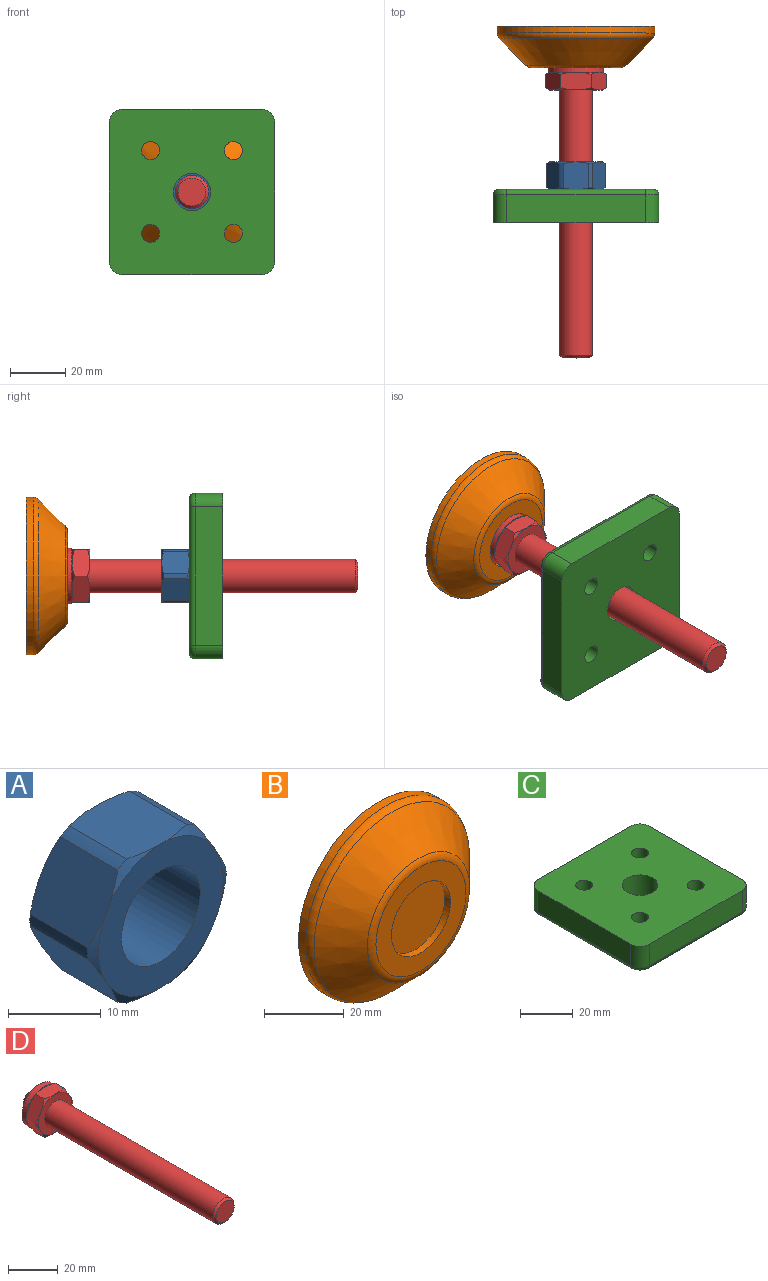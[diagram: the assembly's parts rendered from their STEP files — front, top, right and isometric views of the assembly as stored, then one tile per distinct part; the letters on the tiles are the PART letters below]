
ASSEMBLY  parts=4 mates=3
PART A: 27 faces, bbox 21.1x10x21.1 mm
  f0: cylinder r=6mm len=12mm, axis (0,-1,0), area 377mm2, adj f23,f24
  f1: plane 10x7.95mm, normal (0.87,0,0.5), area 88mm2, adj f2,f3,f4,f5,f19,f21
  f2: cone r=5.28mm half-angle=60deg, axis (0,-1,0), area 5.2mm2, adj f1,f4,f6,f24
  f3: cone r=5.28mm half-angle=60deg, axis (0,-1,0), area 5.2mm2, adj f1,f21,f22,f24
  f4: cylinder r=10.55mm len=8.79mm, axis (0,-1,0), area 13.7mm2, adj f1,f2,f5,f6
  f5: cone r=5.28mm half-angle=60deg, axis (0,1,0), area 5.2mm2, adj f1,f4,f6,f23
  f6: plane 10x7.95mm, normal (0.87,0,-0.5), area 88mm2, adj f2,f4,f5,f7,f8,f9
  f7: cone r=5.28mm half-angle=60deg, axis (0,-1,0), area 5.2mm2, adj f6,f8,f10,f24
  f8: cylinder r=10.55mm len=8.79mm, axis (0,-1,0), area 13.7mm2, adj f6,f7,f9,f10
  f9: cone r=5.28mm half-angle=60deg, axis (0,1,0), area 5.2mm2, adj f6,f8,f10,f23
  f10: plane 10x9.18mm, normal (0,0,-1), area 88mm2, adj f7,f8,f9,f11,f12,f13
  f11: cone r=5.28mm half-angle=60deg, axis (0,-1,0), area 5.2mm2, adj f10,f12,f14,f24
  f12: cylinder r=10.55mm len=8.79mm, axis (0,-1,0), area 13.7mm2, adj f10,f11,f13,f14
  f13: cone r=5.28mm half-angle=60deg, axis (0,1,0), area 5.2mm2, adj f10,f12,f14,f23
  f14: plane 10x7.95mm, normal (-0.87,0,-0.5), area 88mm2, adj f11,f12,f13,f15,f16,f17
  f15: cone r=5.28mm half-angle=60deg, axis (0,-1,0), area 5.2mm2, adj f14,f16,f18,f24
  f16: cylinder r=10.55mm len=8.79mm, axis (0,-1,0), area 13.7mm2, adj f14,f15,f17,f18
  f17: cone r=5.28mm half-angle=60deg, axis (0,1,0), area 5.2mm2, adj f14,f16,f18,f23
  f18: plane 10x7.95mm, normal (-0.87,0,0.5), area 88mm2, adj f15,f16,f17,f20,f25,f26
  f19: cone r=5.28mm half-angle=60deg, axis (0,1,0), area 5.2mm2, adj f1,f21,f22,f23
  f20: cone r=5.28mm half-angle=60deg, axis (0,1,0), area 5.2mm2, adj f18,f22,f23,f26
  f21: cylinder r=10.55mm len=8.79mm, axis (0,-1,0), area 13.7mm2, adj f1,f3,f19,f22
  f22: plane 10x9.18mm, normal (0,0,1), area 88mm2, adj f3,f19,f20,f21,f25,f26
  f23: plane 19x19mm, normal (0,-1,0), area 170.4mm2, adj f0,f5,f9,f13,f17,f19,f20
  f24: plane 19x19mm, normal (0,1,0), area 170.4mm2, adj f0,f2,f3,f7,f11,f15,f25
  f25: cone r=5.28mm half-angle=60deg, axis (0,-1,0), area 5.2mm2, adj f18,f22,f24,f26
  f26: cylinder r=10.55mm len=8.79mm, axis (0,-1,0), area 13.7mm2, adj f18,f20,f22,f25
PART B: 8 faces, bbox 61.7x15x61.7 mm
  f0: cylinder r=28.5mm len=57mm, axis (0,1,0), area 449mm2, adj f1,f7
  f1: torus R=25.5mm, axis (0,1,0), area 417.5mm2, adj f0,f2
  f2: cone r=22.88mm half-angle=45deg, axis (0,1,0), area 1929.5mm2, adj f1,f3
  f3: torus R=16.01mm, axis (0,1,0), area 253.5mm2, adj f2,f6
  f4: cylinder r=10.5mm len=21mm, axis (0,1,0), area 131.9mm2, adj f5,f6
  f5: plane 21x21mm, normal (0,-1,0), area 346.4mm2, adj f4
  f6: plane 32.01x32.01mm, normal (0,-1,0), area 458.6mm2, adj f3,f4
  f7: plane 57x57mm, normal (0,1,0), area 2551.8mm2, adj f0
PART C: 31 faces, bbox 60.8x60.8x12 mm
  f0: cylinder r=3.25mm len=6.5mm, axis (0,0,-1), area 122.5mm2, adj f3,f7
  f1: plane 50x10mm, normal (0,-1,0), area 500mm2, adj f3,f5,f8,f20
  f2: plane 50x10mm, normal (1,0,0), area 500mm2, adj f3,f5,f10,f13
  f3: plane 60x60mm, normal (0,0,1), area 3302.7mm2, adj f0,f1,f2,f5,f11,f12,f13,f18
  f4: plane 56x56mm, normal (0,0,-1), area 2605mm2, adj f6,f8,f9,f10,f14,f16,f17,f21
  f5: cylinder r=5mm len=10mm, axis (0,0,1), area 78.5mm2, adj f1,f2,f3,f9
  f6: cylinder r=5.5mm len=11mm, axis (0,0,-1), area 207.3mm2, adj f4,f7
  f7: plane 11x11mm, normal (0,0,-1), area 61.9mm2, adj f0,f6
  f8: cylinder r=2mm len=50mm, axis (1,0,0), area 157.1mm2, adj f1,f4,f9,f24
  f9: torus R=3mm, axis (0,0,1), area 21.1mm2, adj f4,f5,f8,f10
  f10: cylinder r=2mm len=50mm, axis (0,1,0), area 157.1mm2, adj f2,f4,f9,f16
  f11: cylinder r=3.25mm len=6.5mm, axis (0,0,-1), area 122.5mm2, adj f3,f15
  f12: plane 50x10mm, normal (0,1,0), area 500mm2, adj f3,f13,f17,f26
  f13: cylinder r=5mm len=10mm, axis (0,0,1), area 78.5mm2, adj f2,f3,f12,f16
  f14: cylinder r=5.5mm len=11mm, axis (0,0,-1), area 207.3mm2, adj f4,f15
  f15: plane 11x11mm, normal (0,0,-1), area 61.9mm2, adj f11,f14
  f16: torus R=3mm, axis (0,0,1), area 21.1mm2, adj f4,f10,f13,f17
  f17: cylinder r=2mm len=50mm, axis (-1,0,0), area 157.1mm2, adj f4,f12,f16,f29
  f18: cylinder r=3.25mm len=6.5mm, axis (0,0,-1), area 122.5mm2, adj f3,f22
  f19: plane 50x10mm, normal (-1,0,0), area 500mm2, adj f3,f20,f23,f26
  f20: cylinder r=5mm len=10mm, axis (0,0,1), area 78.5mm2, adj f1,f3,f19,f24
  f21: cylinder r=5.5mm len=11mm, axis (0,0,-1), area 207.3mm2, adj f4,f22
  f22: plane 11x11mm, normal (0,0,-1), area 61.9mm2, adj f18,f21
  f23: cylinder r=2mm len=50mm, axis (0,-1,0), area 157.1mm2, adj f4,f19,f24,f29
  f24: torus R=3mm, axis (0,0,1), area 21.1mm2, adj f4,f8,f20,f23
  f25: cylinder r=3.25mm len=6.5mm, axis (0,0,-1), area 122.5mm2, adj f3,f28
  f26: cylinder r=5mm len=10mm, axis (0,0,1), area 78.5mm2, adj f3,f12,f19,f29
  f27: cylinder r=5.5mm len=11mm, axis (0,0,-1), area 207.3mm2, adj f4,f28
  f28: plane 11x11mm, normal (0,0,-1), area 61.9mm2, adj f25,f27
  f29: torus R=3mm, axis (0,0,1), area 21.1mm2, adj f4,f17,f23,f26
  f30: cylinder r=6.75mm len=13.5mm, axis (0,0,-1), area 508.9mm2, adj f3,f4
PART D: 26 faces, bbox 21.9x112.7x21.9 mm
  f0: sphere r=6mm, area 252.6mm2, adj f10
  f1: cone r=10.23mm half-angle=60deg, axis (0,1,0), area 33.7mm2, adj f4,f5,f14,f15,f16,f17,f18,f19
  f2: cylinder r=6mm len=96.05mm, axis (0,1,0), area 3621.1mm2, adj f3,f24
  f3: cone r=5.53mm half-angle=45deg, axis (0,1,0), area 46.5mm2, adj f2,f23
  f4: cylinder r=10.97mm len=4.8mm, axis (0,1,0), area 0mm2, adj f1,f6,f19,f20
  f5: cylinder r=10.97mm len=4.8mm, axis (0,1,0), area 0mm2, adj f1,f6,f14,f15
  f6: cone r=10.23mm half-angle=60deg, axis (0,-1,0), area 33.7mm2, adj f4,f5,f12,f14,f15,f16,f17,f18
  f7: cylinder r=10mm len=20mm, axis (0,1,0), area 157.1mm2, adj f12,f13
  f8: cylinder r=6.5mm len=13mm, axis (0,1,0), area 102.1mm2, adj f11,f13
  f9: cylinder r=6mm len=12mm, axis (0,1,0), area 94.2mm2, adj f10,f11
  f10: plane 12x12mm, normal (0,1,0), area 1.5mm2, adj f0,f9
  f11: plane 13x13mm, normal (0,1,0), area 19.6mm2, adj f8,f9
  f12: plane 20x20mm, normal (0,-1,0), area 30.6mm2, adj f6,f7
  f13: plane 20x20mm, normal (0,1,0), area 181.4mm2, adj f7,f8
  f14: plane 9.5x7.31mm, normal (0.87,0,0.5), area 64.9mm2, adj f1,f5,f6,f25
  f15: plane 9.5x7.31mm, normal (0.87,0,-0.5), area 64.9mm2, adj f1,f5,f6,f16
  f16: cylinder r=10.97mm len=4.8mm, axis (0,1,0), area 0mm2, adj f1,f6,f15,f17
  f17: plane 10.97x7.31mm, normal (0,0,-1), area 64.9mm2, adj f1,f6,f16,f18
  f18: cylinder r=10.97mm len=4.8mm, axis (0,1,0), area 0mm2, adj f1,f6,f17,f19
  f19: plane 9.5x7.31mm, normal (-0.87,0,-0.5), area 64.9mm2, adj f1,f4,f6,f18
  f20: plane 9.5x7.31mm, normal (-0.87,0,0.5), area 64.9mm2, adj f1,f4,f6,f21
  f21: cylinder r=10.97mm len=4.8mm, axis (0,1,0), area 0mm2, adj f1,f6,f20,f22
  f22: plane 10.97x7.31mm, normal (0,0,1), area 64.9mm2, adj f1,f6,f21,f25
  f23: plane 10.11x10.11mm, normal (0,-1,0), area 80.2mm2, adj f3
  f24: plane 19x19mm, normal (0,-1,0), area 170.4mm2, adj f1,f2
  f25: cylinder r=10.97mm len=4.8mm, axis (0,1,0), area 0mm2, adj f1,f6,f14,f22
PLACE A t=(0,-9.15,0)mm
PLACE B at identity
PLACE C rot(axis=(1,0,0),90deg) t=(0,-9.15,0)mm
PLACE D t=(0,-0.12,0)mm
MATE fastened D.f1 <-> B.f0  axis (0,1,0) through (0,35.88,0)mm
MATE fastened A.f0 <-> C.f30  axis (0,-1,0) through (0,-9.15,0)mm
MATE fastened C.f30 <-> D.f1  axis (0,-1,0) through (0,-21.15,0)mm
